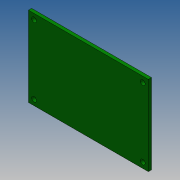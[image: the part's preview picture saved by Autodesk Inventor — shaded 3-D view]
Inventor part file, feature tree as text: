
AUTODESK INVENTOR PART (.ipt)
format: ipt  version: 2017 (Build 210142000, 142)  size: 88,576 bytes
history: native  units: mm
features: other x1, extrude x1, sketch x1
ambient origin geometry x8: Origin, YZ Plane, XZ Plane, XY Plane, X Axis, Y Axis, Z Axis, Center Point
bodies: Body1 (feature_tree)
feature tree (3):
  other  "Sólido1"
  extrude  "Extrusión1"  Depth=2.0mm
  sketch  "Boceto1"  dims[d0=3.0mm d1=3.5mm d2=50.0mm d3=75.0mm d4=2.0mm d5=0.0mm d6=43.0mm d7=68.0mm]
